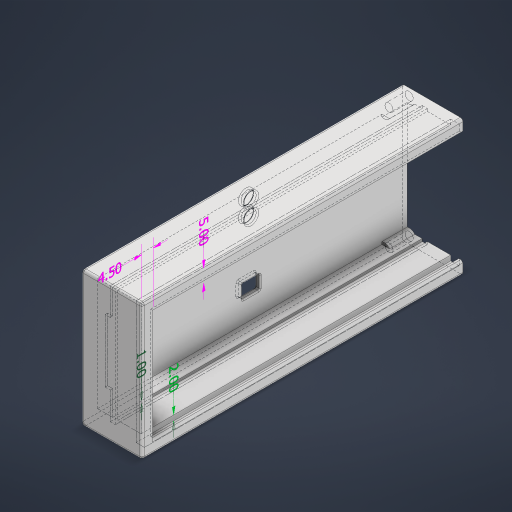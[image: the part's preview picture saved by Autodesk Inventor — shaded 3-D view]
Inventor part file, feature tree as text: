
AUTODESK INVENTOR PART (.ipt)
format: ipt  version: 2023 (Build 270158000, 158)  size: 432,128 bytes
history: native  units: mm
features: other x9, sketch x9, extrude x9, reference x9, projected_geometry x5, chamfer x2, fillet x2, plane x1
ambient origin geometry x8: Origin, YZ Plane, XZ Plane, XY Plane, X Axis, Y Axis, Z Axis, Center Point
bodies: Solid1 (feature_tree)
feature tree (46):
  other  "Annotations"
  sketch  "Sketch1"  dims[d0=0.15mm d1=0.15mm]
  plane  "Work Plane1"
  extrude  "Extrusion1"  Depth=0.15mm
  extrude  "Extrusion2"  Depth=0.15mm
  extrude  "Extrusion3"  Depth=0.15mm
  extrude  "Extrusion4"  Depth=6.0mm
  extrude  "Extrusion5"  Depth=3.325mm
  extrude  "Extrusion6"  Depth=1.5mm
  extrude  "Extrusion7"  Depth=2.0mm
  chamfer  "Chamfer2"  Distance=5.0mm
  extrude  "Extrusion8"  Depth=2.0mm
  fillet  "Fillet1"  Radius=10.0mm
  fillet  "Fillet2"  Radius=4.5mm
  extrude  "Extrusion9"  Depth=3.5mm TaperAngle=0.0deg
  chamfer  "Chamfer1"  Distance=2.5mm
  reference  "Reference1"
  reference  "Reference2"
  reference  "Reference3"
  reference  "Reference4"
  reference  "Reference5"
  reference  "Reference6"
  reference  "Reference7"
  reference  "Reference8"
  sketch  "Sketch2"  dims[d3=0.15mm d4=0.15mm]
  projected_geometry  "Projected Loop1"
  sketch  "Sketch3"  dims[d5=0.15mm d6=0.15mm]
  projected_geometry  "Projected Loop2"
  sketch  "Sketch4"  dims[d7=0.15mm d8=6.0mm]
  projected_geometry  "Projected Loop3"
  sketch  "Sketch5"  dims[d9=2.0mm d10=3.325mm]
  projected_geometry  "Projected Loop4"
  sketch  "Sketch6"  dims[d11=2.5mm d12=1.5mm]
  sketch  "Sketch7"  dims[d13=5.0mm d14=2.0mm]
  projected_geometry  "Projected Loop5"
  sketch  "Sketch8"  dims[d15=2.5mm]
  reference  "Reference9"
  sketch  "Sketch9"  dims[d16=1.5mm d17=5.0mm d18=2.0mm d19=10.0mm d20=0.0mm d21=4.5mm d22=0.0mm d35=3.5mm d36=0.0mm d37=2.5mm d38=0.0mm d39=0.5mm d40=0.0mm d41=3.6mm d42=1.0mm d43=3.6mm d44=1.0mm d45=10.0mm d46=0.0mm d47=3.2mm d48=3.2mm d49=8.0mm d50=0.0mm d51=0.75mm d52=2.0mm d53=45.0deg d54=0.75mm d55=2.0mm d56=45.0deg d61=3.0mm d62=1.5mm d63=2.0mm d64=34.75mm d65=5.0mm d66=5.0mm d67=6.05mm d68=5.33mm d69=0.0mm d70=0.0mm d71=1.0mm d72=0.5mm d73=2.0mm d74=25.0mm d75=0.0mm d76=0.0mm d23=8.440004mm d24=1.260865mm d25=5.0mm d26=8.249104mm d27=7.253461mm d28=4.5mm d29=0.939263mm d30=8.743663mm d31=1.0mm d32=1.007619mm d33=8.65459mm d34=2.0mm]
  other  "<userpath>\Documents\Assembly1.iam"
  other  "Assembly1.iam"
  other  "Clock Main PCB:1"
  other  "V1.0 Lid:1"
  other  "Linear Dimension 1"
  other  "Linear Dimension 2"
  other  "Linear Dimension 3"
  other  "Linear Dimension 4"
